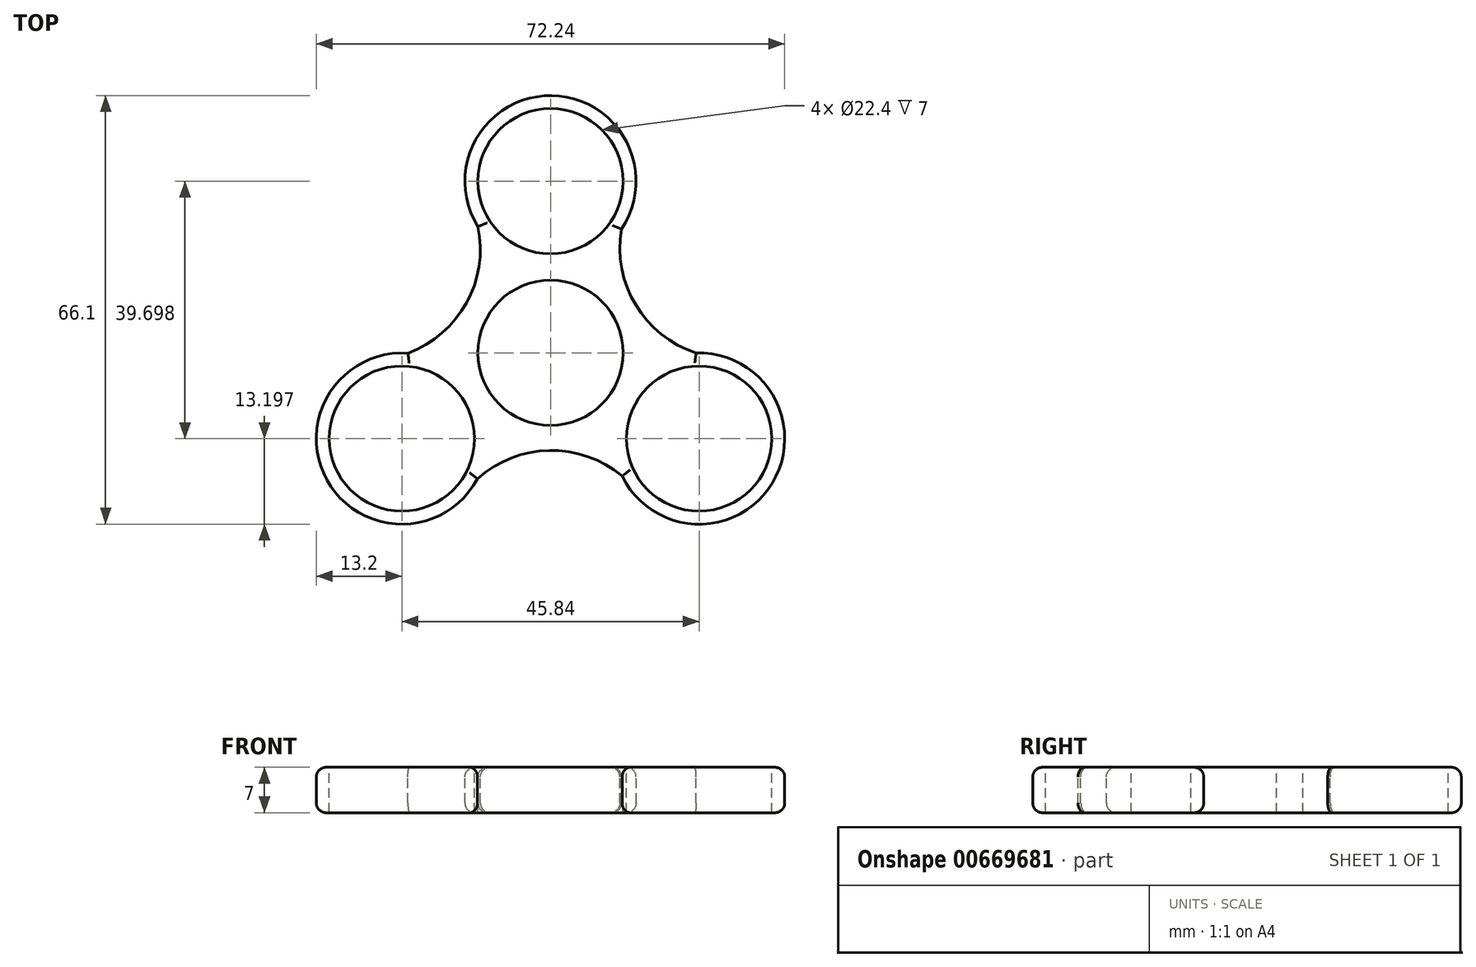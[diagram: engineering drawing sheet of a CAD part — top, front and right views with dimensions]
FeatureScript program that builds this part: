
annotation { "Feature Type Name" : "Feature", "Feature Type Description" : "" }
export const myFeature = defineFeature(function(context is Context, id is Id, definition is map)
    precondition{}
    {
        {
            var Q0;
            Q0=qCreatedBy(makeId("Top.planeOp"),FACE);
            var sketch = newSketch(context, id + "F0", { "sketchPlane" : qUnion([Q0])});
            skCircle(sketch, "E0", {"center": v(0, 0) * mm, "radius": 11.2 * mm});
            skCircle(sketch, "E1", {"center": v(0, 26.47) * mm, "radius": 11.2 * mm});
            skArc(sketch, "E2", {"start": v(10.94, 19.08) * mm, "mid": v(0.23, 39.66) * mm, "end": v(-11.2, 19.47) * mm});
            skArc(sketch, "E3.1.0", {"start": v(-22, -0.07) * mm, "mid": v(-34.47, -19.63) * mm, "end": v(-11.26, -19.43) * mm});
            skCircle(sketch, "E3.1.1", {"center": v(-22.92, -13.23) * mm, "radius": 11.2 * mm});
            skArc(sketch, "E3.2.0", {"start": v(11.05, -19.01) * mm, "mid": v(34.23, -20.03) * mm, "end": v(22.46, -0.04) * mm});
            skCircle(sketch, "E3.2.1", {"center": v(22.92, -13.23) * mm, "radius": 11.2 * mm});
            skLineSegment(sketch, "E4", {"start": v(-13.22, -7.63) * mm, "end": v(-9.7, -5.6) * mm, "construction": true});
            skLineSegment(sketch, "E5", {"start": v(22.92, -13.23) * mm, "end": v(9.8, -5.43) * mm, "construction": true});
            skArc(sketch, "E6", {"start": v(10.94, 19.08) * mm, "mid": v(13.14, 7.38) * mm, "end": v(22.46, -0.04) * mm});
            skArc(sketch, "E7.1.0", {"start": v(-22, -0.07) * mm, "mid": v(-12.96, 7.7) * mm, "end": v(-11.2, 19.47) * mm});
            skArc(sketch, "E7.2.0", {"start": v(11.05, -19.01) * mm, "mid": v(-0.18, -15.07) * mm, "end": v(-11.26, -19.43) * mm});
            skLineSegment(sketch, "E8.trimOffspring", {"start": v(-9.46, 6) * mm, "end": v(-12.8, 7.99) * mm, "construction": true});
            skLineSegment(sketch, "E9.trimOffspring", {"start": v(0, 0) * mm, "end": v(0.33, 0.19) * mm, "construction": true});
            skLineSegment(sketch, "E10.trimOffspring", {"start": v(9.7, 5.6) * mm, "end": v(13.05, 7.53) * mm, "construction": true});
            skSolve(sketch);
        }
        {
            var Q0;
            Q0=makeQuery(id+"F0.imprint","IMPRINT",FACE,{"disambiguationData":[TD([[makeQuery(id+"F0.imprint","IMPRINT",EDGE,{"derivedFrom":sQuery(id+"F0.wireOp",EDGE,"E0")}),-1.0]])]});
            extrude(context, id + "F1", {"entities" : qUnion([Q0]), "oppositeDirection" : true, "depth" : 7 * mm, "offsetDistance" : 25 * mm});
        }
        {
            var Q0;
            Q0=makeQuery(id+"F1.opExtrude","CAP_EDGE",EDGE,{"disambiguationData":[OSD([sQuery(id+"F0.wireOp",EDGE,"E7.2.0")])],"isStart":true});
            var Q1;
            Q1=makeQuery(id+"F1.opExtrude","CAP_EDGE",EDGE,{"disambiguationData":[OSD([sQuery(id+"F0.wireOp",EDGE,"E3.1.0")])],"isStart":true});
            var Q2;
            Q2=makeQuery(id+"F1.opExtrude","CAP_EDGE",EDGE,{"disambiguationData":[OSD([sQuery(id+"F0.wireOp",EDGE,"E7.1.0")])],"isStart":true});
            var Q3;
            Q3=makeQuery(id+"F1.opExtrude","CAP_EDGE",EDGE,{"disambiguationData":[OSD([sQuery(id+"F0.wireOp",EDGE,"E2")])],"isStart":true});
            var Q4;
            Q4=makeQuery(id+"F1.opExtrude","CAP_EDGE",EDGE,{"disambiguationData":[OSD([sQuery(id+"F0.wireOp",EDGE,"E3.2.0")])],"isStart":true});
            var Q5;
            Q5=makeQuery(id+"F1.opExtrude","CAP_EDGE",EDGE,{"disambiguationData":[OSD([sQuery(id+"F0.wireOp",EDGE,"E6")])],"isStart":true});
            var Q6;
            Q6=makeQuery(id+"F1.opExtrude","CAP_EDGE",EDGE,{"disambiguationData":[OSD([sQuery(id+"F0.wireOp",EDGE,"E3.2.0")])],"isStart":false});
            var Q7;
            Q7=makeQuery(id+"F1.opExtrude","CAP_EDGE",EDGE,{"disambiguationData":[OSD([sQuery(id+"F0.wireOp",EDGE,"E7.2.0")])],"isStart":false});
            var Q8;
            Q8=makeQuery(id+"F1.opExtrude","CAP_EDGE",EDGE,{"disambiguationData":[OSD([sQuery(id+"F0.wireOp",EDGE,"E3.1.0")])],"isStart":false});
            var Q9;
            Q9=makeQuery(id+"F1.opExtrude","CAP_EDGE",EDGE,{"disambiguationData":[OSD([sQuery(id+"F0.wireOp",EDGE,"E2")])],"isStart":false});
            var Q10;
            Q10=makeQuery(id+"F1.opExtrude","CAP_EDGE",EDGE,{"disambiguationData":[OSD([sQuery(id+"F0.wireOp",EDGE,"E6")])],"isStart":false});
            var Q11;
            Q11=makeQuery(id+"F1.opExtrude","CAP_EDGE",EDGE,{"disambiguationData":[OSD([sQuery(id+"F0.wireOp",EDGE,"E7.1.0")])],"isStart":false});
            fillet(context, id + "F2", {"entities" : qUnion([Q0, Q1, Q2, Q3, Q4, Q5, Q6, Q7, Q8, Q9, Q10, Q11]), "radius" : 1.5 * mm, "tangentPropagation" : true, "allowEdgeOverflow" : false});
        }
    });
